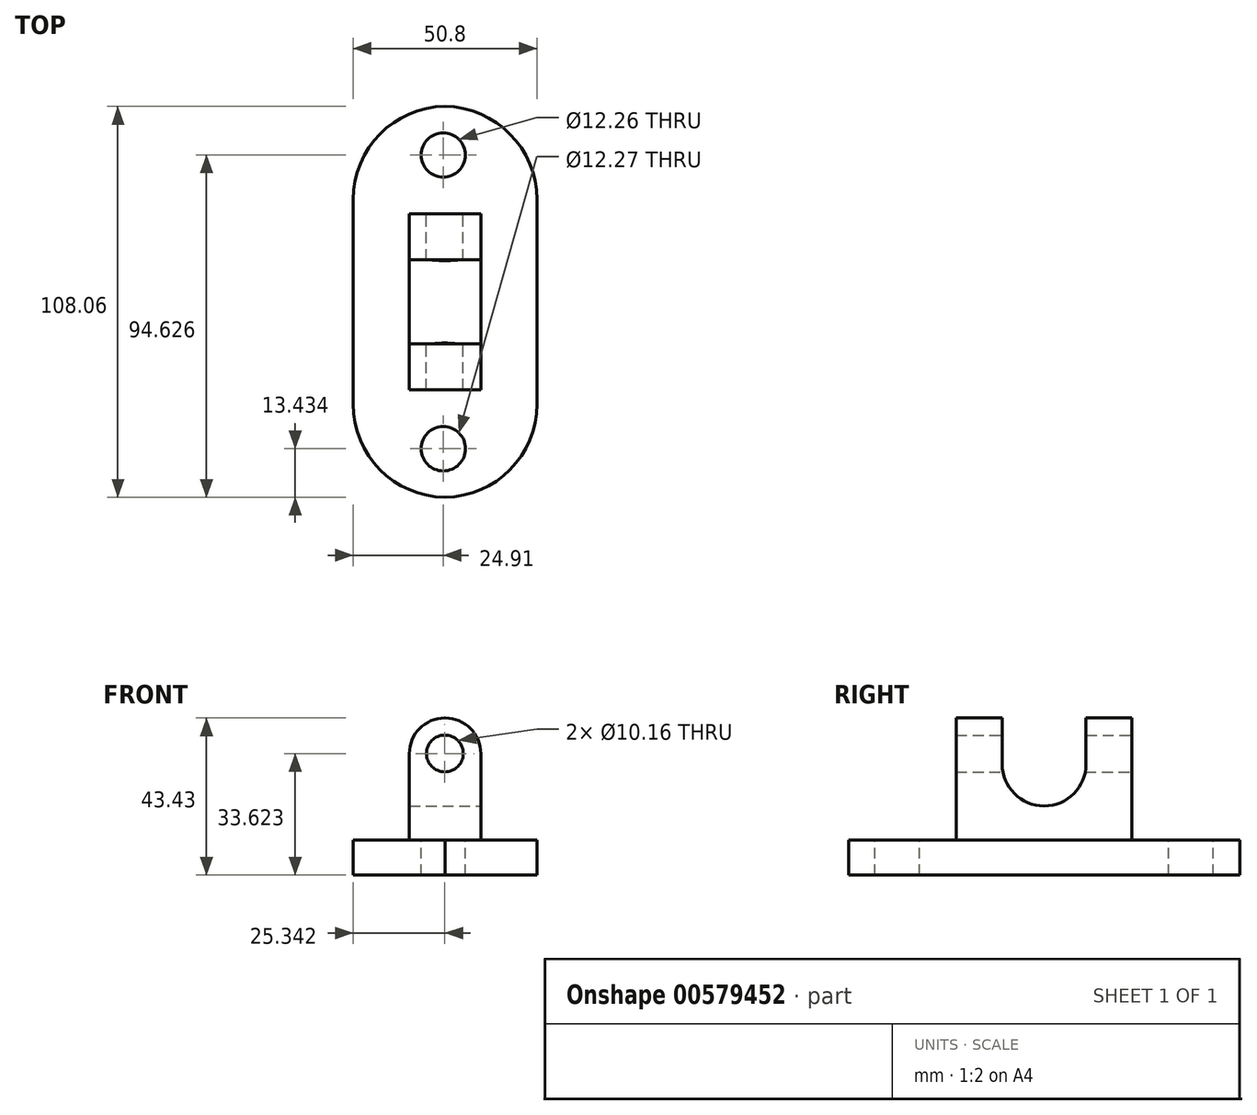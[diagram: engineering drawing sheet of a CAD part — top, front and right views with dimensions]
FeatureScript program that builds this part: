
annotation { "Feature Type Name" : "Feature", "Feature Type Description" : "" }
export const myFeature = defineFeature(function(context is Context, id is Id, definition is map)
    precondition{}
    {
        {
            var Q0;
            Q0=qCreatedBy(makeId("Top.planeOp"),FACE);
            var sketch = newSketch(context, id + "F0", { "sketchPlane" : qUnion([Q0])});
            skLineSegment(sketch, "E0.bottom", {"start": v(-24.9, 54.03) * mm, "end": v(25.9, 54.03) * mm});
            skLineSegment(sketch, "E0.top", {"start": v(-24.9, -54.03) * mm, "end": v(25.9, -54.03) * mm});
            skLineSegment(sketch, "E0.left", {"start": v(-24.9, 54.03) * mm, "end": v(-24.9, -54.03) * mm});
            skLineSegment(sketch, "E0.right", {"start": v(25.9, 54.03) * mm, "end": v(25.9, -54.03) * mm});
            skSolve(sketch);
        }
        {
            var Q0;
            Q0=makeQuery(id+"F0.imprint","IMPRINT",FACE,{"disambiguationData":[TD([[makeQuery(id+"F0.imprint","IMPRINT",EDGE,{"derivedFrom":sQuery(id+"F0.wireOp",EDGE,"E0.bottom")}),-1.0]])]});
            extrude(context, id + "F1", {"entities" : qUnion([Q0]), "depth" : 9.65 * mm, "offsetDistance" : 25.4 * mm});
        }
        {
            var Q0;
            Q0=makeQuery(id+"F1.opExtrude","SWEPT_EDGE",EDGE,{"disambiguationData":[OSD([sQuery(id+"F0.wireOp",EDGE,"E0.bottom"),sQuery(id+"F0.wireOp",EDGE,"E0.right")])]});
            var Q1;
            Q1=makeQuery(id+"F1.opExtrude","SWEPT_EDGE",EDGE,{"disambiguationData":[OSD([sQuery(id+"F0.wireOp",EDGE,"E0.bottom"),sQuery(id+"F0.wireOp",EDGE,"E0.left")])]});
            var Q2;
            Q2=makeQuery(id+"F1.opExtrude","SWEPT_EDGE",EDGE,{"disambiguationData":[OSD([sQuery(id+"F0.wireOp",EDGE,"E0.top"),sQuery(id+"F0.wireOp",EDGE,"E0.right")])]});
            var Q3;
            Q3=makeQuery(id+"F1.opExtrude","SWEPT_EDGE",EDGE,{"disambiguationData":[OSD([sQuery(id+"F0.wireOp",EDGE,"E0.top"),sQuery(id+"F0.wireOp",EDGE,"E0.left")])]});
            fillet(context, id + "F2", {"entities" : qUnion([Q0, Q1, Q2, Q3]), "radius" : 25.75 * mm, "tangentPropagation" : true, "allowEdgeOverflow" : false});
        }
        {
            var Q0;
            Q0=makeQuery(id+"F1.opExtrude","CAP_FACE",FACE,{"disambiguationData":[OSD([sQuery(id+"F0.wireOp",EDGE,"E0.bottom"),sQuery(id+"F0.wireOp",EDGE,"E0.top"),sQuery(id+"F0.wireOp",EDGE,"E0.left"),sQuery(id+"F0.wireOp",EDGE,"E0.right")])],"isStart":false});
            var sketch = newSketch(context, id + "F3", { "sketchPlane" : qUnion([Q0])});
            skCircle(sketch, "E1", {"center": v(0, 40.6) * mm, "radius": 6.13 * mm});
            skCircle(sketch, "E2", {"center": v(0, -40.6) * mm, "radius": 6.13 * mm});
            skSolve(sketch);
        }
        {
            var Q0;
            Q0=makeQuery(id+"F3.imprint","IMPRINT",FACE,{"disambiguationData":[TD([[makeQuery(id+"F3.imprint","IMPRINT",EDGE,{"derivedFrom":sQuery(id+"F3.wireOp",EDGE,"E2")}),1.0]])]});
            var Q1;
            Q1=makeQuery(id+"F3.imprint","IMPRINT",FACE,{"disambiguationData":[TD([[makeQuery(id+"F3.imprint","IMPRINT",EDGE,{"derivedFrom":sQuery(id+"F3.wireOp",EDGE,"E1")}),1.0]])]});
            extrude(context, id + "F4", {"entities" : qUnion([Q0, Q1]), "operationType" : NewBodyOperationType.REMOVE, "endBound" : BoundingType.THROUGH_ALL, "oppositeDirection" : true, "depth" : 25.4 * mm, "offsetDistance" : 25.4 * mm});
        }
        {
            var Q0;
            Q0=makeQuery(id+"F1.opExtrude","CAP_FACE",FACE,{"disambiguationData":[OSD([sQuery(id+"F0.wireOp",EDGE,"E0.bottom"),sQuery(id+"F0.wireOp",EDGE,"E0.top"),sQuery(id+"F0.wireOp",EDGE,"E0.left"),sQuery(id+"F0.wireOp",EDGE,"E0.right")])],"isStart":false});
            var sketch = newSketch(context, id + "F5", { "sketchPlane" : qUnion([Q0])});
            skLineSegment(sketch, "E3.bottom", {"start": v(-9.38, 24.3) * mm, "end": v(10.36, 24.3) * mm});
            skLineSegment(sketch, "E3.top", {"start": v(-9.38, -24.3) * mm, "end": v(10.36, -24.3) * mm});
            skLineSegment(sketch, "E3.left", {"start": v(-9.38, 24.3) * mm, "end": v(-9.38, -24.3) * mm});
            skLineSegment(sketch, "E3.right", {"start": v(10.36, 24.3) * mm, "end": v(10.36, -24.3) * mm});
            skSolve(sketch);
        }
        {
            var Q0;
            Q0=makeQuery(id+"F5.imprint","IMPRINT",FACE,{"disambiguationData":[TD([[makeQuery(id+"F5.imprint","IMPRINT",EDGE,{"derivedFrom":sQuery(id+"F5.wireOp",EDGE,"E3.bottom")}),-1.0]])]});
            extrude(context, id + "F6", {"entities" : qUnion([Q0]), "operationType" : NewBodyOperationType.ADD, "depth" : 33.78 * mm, "offsetDistance" : 25.4 * mm});
        }
        {
            var Q0;
            Q0=makeQuery(id+"F6.opExtrude","SWEPT_FACE",FACE,{"disambiguationData":[OSD([sQuery(id+"F5.wireOp",EDGE,"E3.right")])]});
            var sketch = newSketch(context, id + "F7", { "sketchPlane" : qUnion([Q0])});
            skLineSegment(sketch, "E4.bottom", {"start": v(-11.6, 43.43) * mm, "end": v(11.6, 43.43) * mm});
            skLineSegment(sketch, "E4.top", {"start": v(-11.6, 30.73) * mm, "end": v(11.6, 30.73) * mm});
            skLineSegment(sketch, "E4.left", {"start": v(-11.6, 43.43) * mm, "end": v(-11.6, 30.73) * mm});
            skLineSegment(sketch, "E4.right", {"start": v(11.6, 43.43) * mm, "end": v(11.6, 30.73) * mm});
            skArc(sketch, "E5", {"start": v(-11.6, 30.73) * mm, "mid": v(0, 19.13) * mm, "end": v(11.6, 30.73) * mm});
            skSolve(sketch);
        }
        {
            var Q0;
            Q0=makeQuery(id+"F7.imprint","IMPRINT",FACE,{"disambiguationData":[TD([[makeQuery(id+"F7.imprint","IMPRINT",EDGE,{"derivedFrom":sQuery(id+"F7.wireOp",EDGE,"E4.bottom")}),1.0]])]});
            var Q1;
            Q1=makeQuery(id+"F7.imprint","IMPRINT",FACE,{"disambiguationData":[TD([[makeQuery(id+"F7.imprint","IMPRINT",EDGE,{"derivedFrom":sQuery(id+"F7.wireOp",EDGE,"E4.top")}),-1.0]])]});
            extrude(context, id + "F8", {"entities" : qUnion([Q0, Q1]), "operationType" : NewBodyOperationType.REMOVE, "endBound" : BoundingType.THROUGH_ALL, "oppositeDirection" : true, "depth" : 25.4 * mm, "offsetDistance" : 25.4 * mm});
        }
        {
            var Q0;
            {var subQ0=sQuery(id+"F5.wireOp",EDGE,"E3.bottom");var subQ1=sQuery(id+"F5.wireOp",EDGE,"E3.left");Q0=makeQuery(id+"F8.boolean.opBoolean","SPLIT",EDGE,{"disambiguationData":[TD([makeQuery(id+"F6.opExtrude","SWEPT_FACE",FACE,{"disambiguationData":[OSD([subQ0])]})])],"derivedFrom":makeQuery(id+"F6.opExtrude","CAP_EDGE",EDGE,{"disambiguationData":[OSD([subQ1])],"isStart":false})});}
            var Q1;
            {var subQ0=sQuery(id+"F5.wireOp",EDGE,"E3.bottom");var subQ1=sQuery(id+"F5.wireOp",EDGE,"E3.right");Q1=makeQuery(id+"F8.boolean.opBoolean","SPLIT",EDGE,{"disambiguationData":[TD([makeQuery(id+"F6.opExtrude","SWEPT_FACE",FACE,{"disambiguationData":[OSD([subQ0])]})])],"derivedFrom":makeQuery(id+"F6.opExtrude","CAP_EDGE",EDGE,{"disambiguationData":[OSD([subQ1])],"isStart":false})});}
            var Q2;
            {var subQ0=sQuery(id+"F5.wireOp",EDGE,"E3.left");var subQ1=sQuery(id+"F5.wireOp",EDGE,"E3.top");Q2=makeQuery(id+"F8.boolean.opBoolean","SPLIT",EDGE,{"disambiguationData":[TD([makeQuery(id+"F6.opExtrude","SWEPT_FACE",FACE,{"disambiguationData":[OSD([subQ1])]})])],"derivedFrom":makeQuery(id+"F6.opExtrude","CAP_EDGE",EDGE,{"disambiguationData":[OSD([subQ0])],"isStart":false})});}
            var Q3;
            {var subQ0=sQuery(id+"F5.wireOp",EDGE,"E3.right");var subQ1=sQuery(id+"F5.wireOp",EDGE,"E3.top");Q3=makeQuery(id+"F8.boolean.opBoolean","SPLIT",EDGE,{"disambiguationData":[TD([makeQuery(id+"F6.opExtrude","SWEPT_FACE",FACE,{"disambiguationData":[OSD([subQ1])]})])],"derivedFrom":makeQuery(id+"F6.opExtrude","CAP_EDGE",EDGE,{"disambiguationData":[OSD([subQ0])],"isStart":false})});}
            fillet(context, id + "F9", {"entities" : qUnion([Q0, Q1, Q2, Q3]), "radius" : 9.8 * mm, "tangentPropagation" : true, "allowEdgeOverflow" : false});
        }
        {
            var Q0;
            Q0=makeQuery(id+"F6.opExtrude","SWEPT_FACE",FACE,{"disambiguationData":[OSD([sQuery(id+"F5.wireOp",EDGE,"E3.bottom")])]});
            var sketch = newSketch(context, id + "F10", { "sketchPlane" : qUnion([Q0])});
            skCircle(sketch, "E6", {"center": v(-0.43, 33.62) * mm, "radius": 5.08 * mm});
            skSolve(sketch);
        }
        {
            var Q0;
            Q0=makeQuery(id+"F10.imprint","IMPRINT",FACE,{"disambiguationData":[TD([[makeQuery(id+"F10.imprint","IMPRINT",EDGE,{"derivedFrom":sQuery(id+"F10.wireOp",EDGE,"E6")}),1.0]])]});
            extrude(context, id + "F11", {"entities" : qUnion([Q0]), "operationType" : NewBodyOperationType.REMOVE, "endBound" : BoundingType.THROUGH_ALL, "oppositeDirection" : true, "depth" : 25.4 * mm, "offsetDistance" : 25.4 * mm});
        }
    });
